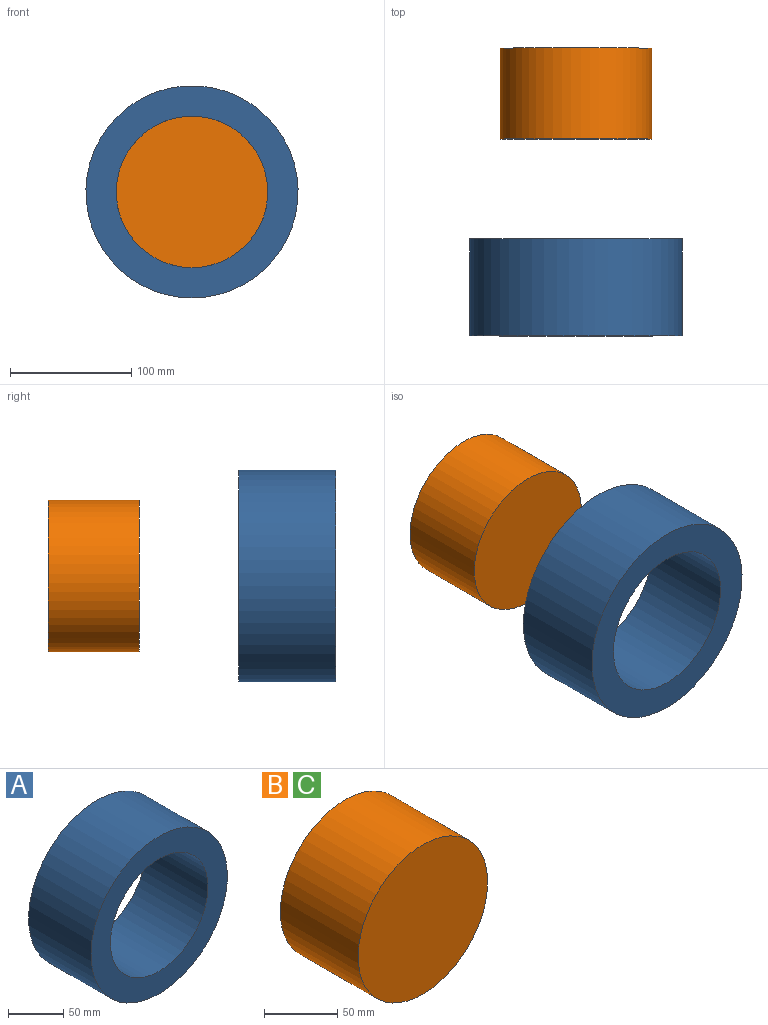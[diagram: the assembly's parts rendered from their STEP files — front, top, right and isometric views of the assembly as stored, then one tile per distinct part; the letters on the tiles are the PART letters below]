
ASSEMBLY  parts=3 mates=3
PART A: 4 faces, bbox 175x80x175 mm
  f0: cylinder r=62.5mm len=125mm, axis (0,1,0), area 31415.9mm2, adj f2,f3
  f1: cylinder r=87.5mm len=175mm, axis (0,1,0), area 43982.3mm2, adj f2,f3
  f2: plane 175x175mm, normal (0,-1,0), area 11781mm2, adj f0,f1
  f3: plane 175x175mm, normal (0,1,0), area 11781mm2, adj f0,f1
PART B: 3 faces, bbox 124.9x75x124.9 mm
  f0: cylinder r=62.45mm len=124.9mm, axis (0,1,0), area 29428.9mm2, adj f1,f2
  f1: plane 124.9x124.9mm, normal (0,-1,0), area 12252.2mm2, adj f0
  f2: plane 124.9x124.9mm, normal (0,1,0), area 12252.2mm2, adj f0
PART C: same geometry as B
PLACE A t=(-180.23,-448.11,244.48)mm
PLACE B t=(-180.23,-290.73,244.48)mm
PLACE C t=(-180.23,-290.73,244.48)mm
MATE slider A.f1 <-> B.f0  axis (0,1,0) through (-180.23,-448.11,244.48)mm
MATE fastened C.f0 <-> B.f0  axis (0,1,0) through (-180.23,-290.73,244.48)mm
MATE parallel B.f0 <-> A.f0  axis (0,1,0) through (-180.23,-290.73,244.48)mm
